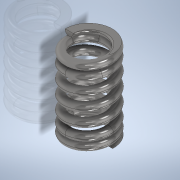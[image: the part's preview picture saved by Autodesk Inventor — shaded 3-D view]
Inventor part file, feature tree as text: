
AUTODESK INVENTOR PART (.ipt)
format: ipt  version: 2022 (Build 260153000, 153)  size: 1,011,712 bytes
history: native  units: mm
features: other x41, sketch x31, extrude x8, helix x4, sweep x2
ambient origin geometry x8: Origin, YZ Plane, XZ Plane, XY Plane, X Axis, Y Axis, Z Axis, Center Point
bodies: Solid1 (feature_tree)
feature tree (86):
  other  "Caminho helicoidal principal (direita)"
  other  "Plano de trabalho de seção (direita)"
  other  "Plano de trabalho inicial (direita)"
  other  "Plano de trabalho final (direita)"
  other  "Plano de trabalho de corte final (direita)"
  other  "Plano de trabalho de corte inicial (direita)"
  other  "Plano de trabalho de corte final normal 1 (direita)"
  other  "Plano de trabalho de corte final normal 2 (direita)"
  sweep  "Main Coil Feature(R)"
  other  "Espiral de transição inicial 1 (direita)"
  helix  "Coil  Start Transition 2(R)"  [1 undecoded]
  helix  "Coil  Start Transition 3(R)"  [1 undecoded]
  helix  "Coil  Start Transition 4(R)"  [1 undecoded]
  other  "Espiral de extremidades iniciais (direita)"
  extrude  "Operação de corte inicial (direita)"  Depth=10.0mm
  other  "Espiral de transição final 1 (direita)"
  other  "Espiral de transição final 2 (direita)"
  other  "Espiral de transição final 3 (direita)"
  other  "Espiral de transição final 4 (direita)"
  other  "Espiral final (direita)"
  extrude  "Operação de corte final (direita)"  Depth=10.0mm
  extrude  "Operação de corte de extremidades normais 1 (direita)"  Depth=6.0mm
  extrude  "Plain Ends Cut  2(R)"  Depth=6.0mm
  other  "Caminho helicoidal principal (esquerda)"
  other  "Plano de trabalho de seção (esquerda)"
  other  "Plano de trabalho inicial (esquerda)"
  other  "Plano de trabalho final (esquerda)"
  other  "Plano de trabalho de corte final (esquerda)"
  other  "Plano de trabalho de corte inicial (esquerda)"
  other  "Plano de trabalho de corte de extremidades normais 1 (esquerda)"
  other  "Plano de trabalho de corte de extremidades normais 2 (esquerda)"
  sweep  "Main Coil Feature(L)"
  other  "Espiral de transição inicial 1 (esquerda)"
  other  "Espiral de transição inicial 2 (esquerda)"
  other  "Espiral de transição inicial 3 (esquerda)"
  other  "Espiral de transição inicial 4 (esquerda)"
  other  "Espiral de extremidades iniciais (esquerda)"
  extrude  "Operação de corte inicial (esquerda)"  TaperAngle=0.0deg  [1 undecoded]
  helix  "Coil End Transition 1(L)"  [1 undecoded]
  other  "Espiral de transição final 2 (esquerda)"
  other  "Espiral de transição final 3 (esquerda)"
  other  "Espiral de transição final 4 (esquerda)"
  other  "Espiral final (esquerda)"
  extrude  "Operação de corte final (esquerda)"  Depth=0.25mm
  extrude  "Cut Plain Ends Cut 1(L)"  Depth=10.0mm
  extrude  "Cut Plain Ends Cut 2(L)"  Depth=1.942655mm
  other  "Plano de trabalho baseado em iMate"
  other  "Visualização do centro"
  other  "Vissualiação do eixo X"
  sketch  "Esboço de corte de caminho (direita)"  dims[d0=0.25mm d2=1.684938mm d3=10.0mm d4=32.5mm]
  other  "Srf1"
  sketch  "Esboço de corte helicoidal (direita)"  dims[d5=0.0mm d6=90.0deg d7=90.0deg d8=0.0mm d9=0.0mm d12=1.942655mm d13=-2.508302mm d14=1.0mm]
  sketch  "Esboço helicoidal de transição inicial 1 (direita)"  dims[d15=0.0mm]
  sketch  "Sketch  Start Transition 2(R)"  dims[d16=1.513704mm d17=10.0mm d18=2.5mm d19=0.0mm d20=90.0deg d21=90.0deg d22=0.0mm d23=0.0mm]
  sketch  "Sketch  Start Transition 3(R)"  dims[d24=1.342469mm d25=10.0mm d26=2.5mm d27=0.0mm d28=90.0deg d29=90.0deg d30=0.0mm d31=0.0mm]
  sketch  "Sketch  Start Transition 4(R)"  dims[d32=1.171235mm d33=10.0mm d34=2.5mm d35=0.0mm d36=90.0deg d37=90.0deg d38=0.0mm d39=0.0mm]
  sketch  "Esboço helicoidal de transição final 1 (direita)"  dims[d40=1.0mm d41=10.0mm d42=2.5mm d43=0.0mm d44=90.0deg d45=90.0deg d46=0.0mm d47=0.0mm]
  sketch  "Esboço helicoidal de transição final 2 (direita)"  dims[d48=1.513704mm d49=10.0mm d50=1.875mm d51=0.0mm d52=90.0deg d53=90.0deg d54=0.0mm d55=0.0mm]
  sketch  "Esboço helicoidal de transição final 3 (direita)"  dims[d56=1.342469mm d57=10.0mm d58=1.875mm d59=0.0mm d60=90.0deg d61=90.0deg d62=0.0mm d63=0.0mm]
  sketch  "Esboço helicoidal de transição final 4 (direita)"  dims[d64=1.171235mm d65=10.0mm d66=1.875mm d67=0.0mm d68=90.0deg d69=90.0deg d70=0.0mm d71=0.0mm]
  sketch  "Esboço de extremidades iniciais (direita)"  dims[d72=1.0mm d73=10.0mm d74=1.875mm d75=0.0mm d76=90.0deg d77=90.0deg d78=0.0mm d79=0.0mm d81=10.0mm d82=15.0mm]
  sketch  "Esboço helicoidal final (direita)"  dims[d83=0.0mm d84=90.0deg d85=90.0deg d86=0.0mm d87=0.0mm d88=1.005737mm d89=10.0mm d90=10.0mm]
  sketch  "Esboço de corte final (direita)"  dims[d91=0.0mm d92=90.0deg d93=90.0deg d94=0.0mm d95=0.0mm d96=6.0mm]
  sketch  "Esboço de corte inicial (direita)"  dims[d97=1.005737mm d98=0.0mm d99=6.0mm]
  sketch  "Esboço de corte de caminho (esquerda)"  dims[d100=1.005737mm d101=0.0mm]
  other  "Srf2"
  sketch  "Esboço de corte helicoidal (esquerda)"  dims[d102=0.0mm d103=0.0mm d104=0.0mm d105=0.0mm d106=0.0mm d108=0.0mm d112=0.0mm d113=0.0mm d114=0.0mm d121=0.257154mm]
  sketch  "Esboço helicoidal de transição inicial 1 (esquerda)"  dims[d131=0.0mm d132=0.0mm d133=0.0mm]
  sketch  "Esboço helicoidal de transição inicial 2 (esquerda)"  dims[d134=0.0mm d135=0.25mm]
  sketch  "Esboço helicoidal de transição inicial 3 (esquerda)"  dims[d137=1.684938mm d138=10.0mm d139=32.5mm]
  sketch  "Esboço helicoidal de transição inicial 4 (esquerda)"  dims[d140=0.0mm d141=90.0deg d142=90.0deg d143=0.0mm d144=0.0mm d145=1.942655mm]
  sketch  "Esboço de extremidades iniciais (esquerda)"  dims[d146=-2.508302mm]
  sketch  "Esboço de corte inicial (esquerda)"  dims[d147=0.257154mm]
  sketch  "Esboço helicoidal de transição final 1 (esquerda)"  dims[d148=0.00572mm]
  sketch  "Esboço helicoidal de transição final 2 (esquerda)"  dims[d149=1.0mm]
  other  "Esoço helicoidal de transição final 3 (esquerda)"
  sketch  "Esboço helicoidal de transição final 4 (esquerda)"  dims[d150=0.0mm]
  sketch  "Esboço helicoidal final (esquerda)"  dims[d151=0.0mm]
  sketch  "Esboço de corte final (esquerda)"  dims[d152=1.513704mm d153=10.0mm d154=2.5mm d155=0.0mm d156=90.0deg d157=90.0deg d158=0.0mm d159=0.0mm]
  sketch  "Esboço de corte de extremidades normais 2 (esquerda)"  dims[d160=1.342469mm]
  sketch  "Esboço de corte de extremidades normais 2 (direita)"  dims[d161=10.0mm d162=2.5mm d163=0.0mm d164=90.0deg d165=90.0deg d166=0.0mm d167=0.0mm]
  sketch  "Esboço de corte de extremidades normais 1 (direita)"  dims[d168=1.171235mm]
  sketch  "Esboço de corte de extremidades normais 1 (esquerda)"  dims[d169=10.0mm d170=2.5mm d171=0.0mm d172=90.0deg d173=90.0deg d174=0.0mm d175=0.0mm d176=1.0mm d177=10.0mm d178=2.5mm d179=0.0mm d180=90.0deg d181=90.0deg d182=0.0mm d183=0.0mm d184=10.0mm d185=10.0mm d186=10.0mm d187=10.0mm d188=1.005737mm d189=10.0mm d190=15.0mm d191=0.0mm d192=90.0deg d193=90.0deg d194=0.0mm d195=0.0mm d196=10.0mm d197=6.0mm d198=1.005737mm d199=0.0mm d200=10.0mm d201=1.513704mm d202=10.0mm d203=1.875mm d204=0.0mm d205=90.0deg d206=90.0deg d207=0.0mm d208=0.0mm d209=10.0mm d210=1.342469mm d211=10.0mm d212=1.875mm d213=0.0mm d214=90.0deg d215=90.0deg d216=0.0mm d217=0.0mm d218=1.171235mm d219=10.0mm d220=1.875mm d221=0.0mm d222=90.0deg d223=90.0deg d224=0.0mm d225=0.0mm d226=1.0mm d227=10.0mm d228=1.875mm d229=0.0mm d230=90.0deg d231=90.0deg d232=0.0mm d233=0.0mm d234=10.0mm d235=10.0mm d236=10.0mm d237=1.005737mm d238=10.0mm d239=10.0mm d240=0.0mm d241=90.0deg d242=90.0deg d243=0.0mm d244=0.0mm d245=6.0mm d246=1.005737mm d247=0.0mm d248=10.0mm d249=10.0mm d254=6.0mm d255=10.0mm d256=0.0mm d257=20.0mm d258=-0.00572mm d259=6.0mm d260=10.0mm d261=0.0mm d262=10.0mm d263=6.0mm d264=10.0mm d265=0.0mm d266=10.0mm d267=0.0mm d270=-2.383302mm d271=0.0mm d272=6.0mm d273=10.0mm d274=0.0mm d275=20.0mm d276=-157.079633mm d277=5.0mm d278=5.0mm d279=0.0mm d280=0.0mm]
  other  "Seção inicial do Plano de trabalho"
  other  "Curva básica (direita)"
  other  "Curva básica (esquerda)"
note: 5 required parameter values undecoded (feature->parameter linkage not recoverable at this tier; creation-order binding heuristic only, values carry confidence <= 0.55)
